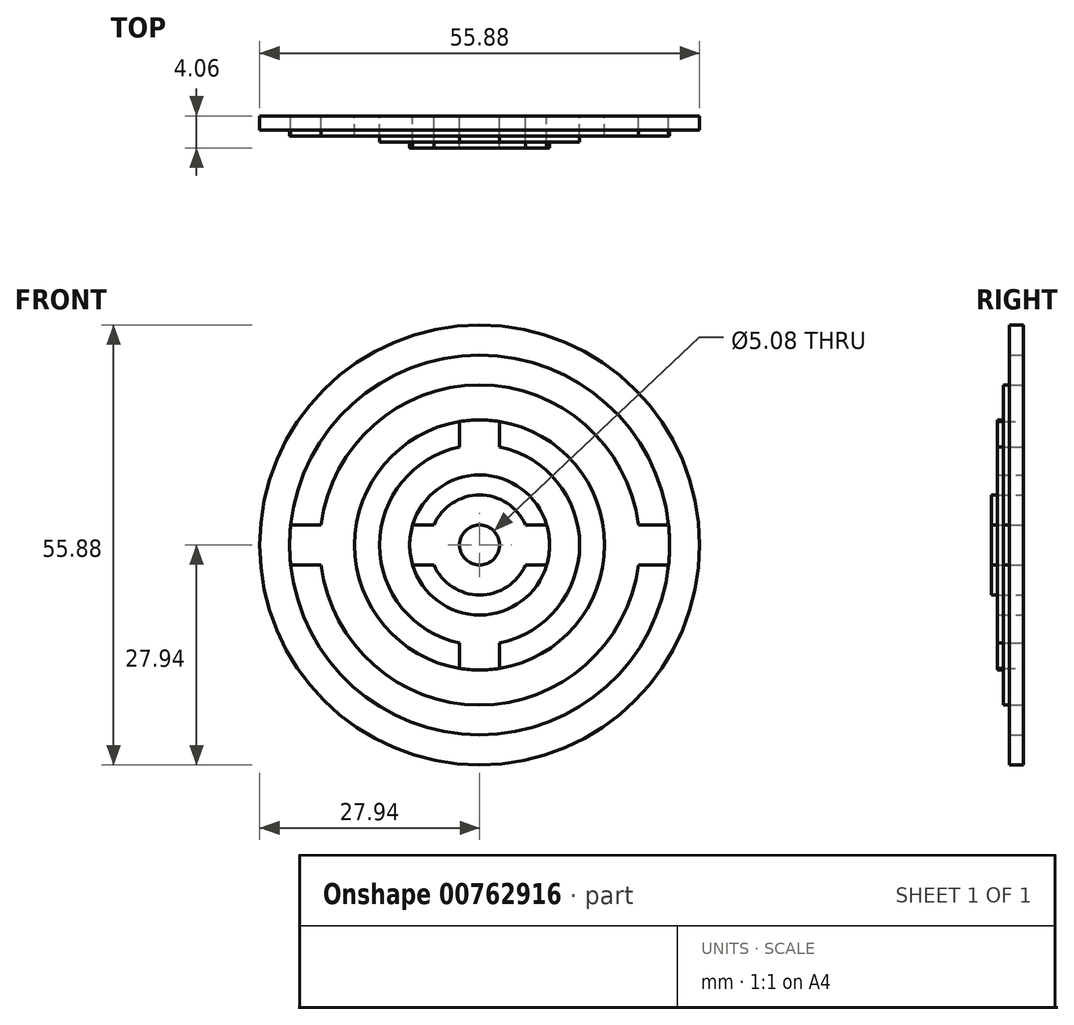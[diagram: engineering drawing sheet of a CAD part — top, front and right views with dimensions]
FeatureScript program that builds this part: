
annotation { "Feature Type Name" : "Feature", "Feature Type Description" : "" }
export const myFeature = defineFeature(function(context is Context, id is Id, definition is map)
    precondition{}
    {
        {
            var Q0;
            Q0=qCreatedBy(makeId("Front.planeOp"),FACE);
            var sketch = newSketch(context, id + "F0", { "sketchPlane" : qUnion([Q0])});
            skCircle(sketch, "E0", {"center": v(0, 0) * mm, "radius": 12.7 * mm});
            skCircle(sketch, "E1", {"center": v(0, 0) * mm, "radius": 20.32 * mm});
            skCircle(sketch, "E2", {"center": v(0, 0) * mm, "radius": 2.54 * mm});
            skCircle(sketch, "E3", {"center": v(0, 0) * mm, "radius": 6.35 * mm});
            skCircle(sketch, "E4", {"center": v(0, 0) * mm, "radius": 27.94 * mm});
            skCircle(sketch, "E5", {"center": v(0, 0) * mm, "radius": 8.9 * mm});
            skCircle(sketch, "E6", {"center": v(0, 0) * mm, "radius": 15.88 * mm});
            skCircle(sketch, "E7", {"center": v(0, 0) * mm, "radius": 24.13 * mm});
            skLineSegment(sketch, "E8", {"start": v(-2.54, -5.82) * mm, "end": v(-2.54, -8.52) * mm});
            skLineSegment(sketch, "E9", {"start": v(2.54, -5.82) * mm, "end": v(2.54, -8.52) * mm});
            skLineSegment(sketch, "E10", {"start": v(5.82, -2.54) * mm, "end": v(8.52, -2.54) * mm});
            skLineSegment(sketch, "E11", {"start": v(-5.82, 2.54) * mm, "end": v(-8.52, 2.54) * mm});
            skLineSegment(sketch, "E12", {"start": v(-5.82, -2.54) * mm, "end": v(-8.52, -2.54) * mm});
            skLineSegment(sketch, "E13.trimOffspring", {"start": v(5.82, 2.54) * mm, "end": v(8.52, 2.54) * mm});
            skLineSegment(sketch, "E14.trimOffspring", {"start": v(2.54, 5.82) * mm, "end": v(2.54, 8.52) * mm});
            skLineSegment(sketch, "E15.trimOffspring", {"start": v(-2.54, 5.82) * mm, "end": v(-2.54, 8.52) * mm});
            skPoint(sketch, "E16.orphan", {"position": v(0, -2.54) * mm});
            skPoint(sketch, "E17.start.orphan", {"position": v(2.54, 0) * mm});
            skPoint(sketch, "E18.orphan", {"position": v(0, 2.54) * mm});
            skPoint(sketch, "E19.start.orphan", {"position": v(-2.54, 0) * mm});
            skLineSegment(sketch, "E20.trimOffspring", {"start": v(-12.44, -2.54) * mm, "end": v(-15.67, -2.54) * mm});
            skLineSegment(sketch, "E21.trimOffspring", {"start": v(-12.44, 2.54) * mm, "end": v(-15.67, 2.54) * mm});
            skLineSegment(sketch, "E22.trimOffspring", {"start": v(-2.54, 12.44) * mm, "end": v(-2.54, 15.67) * mm});
            skLineSegment(sketch, "E23.trimOffspring", {"start": v(2.54, 12.44) * mm, "end": v(2.54, 15.67) * mm});
            skLineSegment(sketch, "E24.trimOffspring", {"start": v(12.44, 2.54) * mm, "end": v(15.67, 2.54) * mm});
            skLineSegment(sketch, "E25.trimOffspring", {"start": v(12.44, -2.54) * mm, "end": v(15.67, -2.54) * mm});
            skLineSegment(sketch, "E26.trimOffspring", {"start": v(20.16, -2.54) * mm, "end": v(24, -2.54) * mm});
            skLineSegment(sketch, "E27.trimOffspring", {"start": v(2.54, -12.44) * mm, "end": v(2.54, -15.67) * mm});
            skLineSegment(sketch, "E28.trimOffspring", {"start": v(-2.54, -12.44) * mm, "end": v(-2.54, -15.67) * mm});
            skLineSegment(sketch, "E29.trimOffspring", {"start": v(20.16, 2.54) * mm, "end": v(24, 2.54) * mm});
            skLineSegment(sketch, "E30.trimOffspring", {"start": v(2.54, 20.16) * mm, "end": v(2.54, 24) * mm});
            skLineSegment(sketch, "E31.trimOffspring", {"start": v(-2.54, 20.16) * mm, "end": v(-2.54, 24) * mm});
            skLineSegment(sketch, "E32.trimOffspring", {"start": v(-20.16, 2.54) * mm, "end": v(-24, 2.54) * mm});
            skLineSegment(sketch, "E33.trimOffspring", {"start": v(-20.16, -2.54) * mm, "end": v(-24, -2.54) * mm});
            skLineSegment(sketch, "E34.trimOffspring", {"start": v(-2.54, -20.16) * mm, "end": v(-2.54, -24) * mm});
            skLineSegment(sketch, "E35.trimOffspring", {"start": v(2.54, -20.16) * mm, "end": v(2.54, -24) * mm});
            skSolve(sketch);
        }
        {
            var Q0;
            Q0=makeQuery(id+"F0.imprint","IMPRINT",FACE,{"disambiguationData":[TD([[makeQuery(id+"F0.imprint","IMPRINT",EDGE,{"derivedFrom":sQuery(id+"F0.wireOp",EDGE,"E2")}),-1.0]])]});
            var Q1;
            {var subQ0=sQuery(id+"F0.wireOp",EDGE,"E11");Q1=makeQuery(id+"F0.imprint","IMPRINT",FACE,{"disambiguationData":[TD([[makeQuery(id+"F0.imprint","IMPRINT",EDGE,{"derivedFrom":subQ0}),1.0]])]});}
            var Q2;
            {var subQ0=sQuery(id+"F0.wireOp",EDGE,"E10");Q2=makeQuery(id+"F0.imprint","IMPRINT",FACE,{"disambiguationData":[TD([[makeQuery(id+"F0.imprint","IMPRINT",EDGE,{"derivedFrom":subQ0}),1.0]])]});}
            extrude(context, id + "F1", {"entities" : qUnion([Q0, Q1, Q2]), "depth" : 4.06 * mm, "offsetDistance" : 25.4 * mm});
        }
        {
            var Q0;
            {var subQ0=sQuery(id+"F0.wireOp",EDGE,"E0");var subQ14=makeQuery(id+"F0.imprint","INTERSECT",VERTEX,{"derivedFrom":[subQ0,sQuery(id+"F0.wireOp",EDGE,"E23.trimOffspring")]});Q0=makeQuery(id+"F0.imprint","IMPRINT",FACE,{"disambiguationData":[TD([[makeQuery(id+"F0.imprint","IMPRINT",EDGE,{"disambiguationData":[TD([[subQ14,1.0]])],"derivedFrom":subQ0}),1.0]])]});}
            var Q1;
            {var subQ0=sQuery(id+"F0.wireOp",EDGE,"E27.trimOffspring");Q1=makeQuery(id+"F0.imprint","IMPRINT",FACE,{"disambiguationData":[TD([[makeQuery(id+"F0.imprint","IMPRINT",EDGE,{"derivedFrom":subQ0}),-1.0]])]});}
            var Q2;
            {var subQ0=sQuery(id+"F0.wireOp",EDGE,"E22.trimOffspring");Q2=makeQuery(id+"F0.imprint","IMPRINT",FACE,{"disambiguationData":[TD([[makeQuery(id+"F0.imprint","IMPRINT",EDGE,{"derivedFrom":subQ0}),-1.0]])]});}
            extrude(context, id + "F2", {"entities" : qUnion([Q0, Q1, Q2]), "operationType" : NewBodyOperationType.ADD, "depth" : 3.3 * mm, "offsetDistance" : 25.4 * mm});
        }
        {
            var Q0;
            {var subQ0=sQuery(id+"F0.wireOp",EDGE,"E1");var subQ2=makeQuery(id+"F0.imprint","INTERSECT",VERTEX,{"derivedFrom":[subQ0,sQuery(id+"F0.wireOp",EDGE,"E29.trimOffspring")]});Q0=makeQuery(id+"F0.imprint","IMPRINT",FACE,{"disambiguationData":[TD([[makeQuery(id+"F0.imprint","IMPRINT",EDGE,{"disambiguationData":[TD([[subQ2,-1.0]])],"derivedFrom":subQ0}),1.0]])]});}
            var Q1;
            {var subQ0=sQuery(id+"F0.wireOp",EDGE,"E26.trimOffspring");Q1=makeQuery(id+"F0.imprint","IMPRINT",FACE,{"disambiguationData":[TD([[makeQuery(id+"F0.imprint","IMPRINT",EDGE,{"derivedFrom":subQ0}),1.0]])]});}
            var Q2;
            {var subQ0=sQuery(id+"F0.wireOp",EDGE,"E32.trimOffspring");Q2=makeQuery(id+"F0.imprint","IMPRINT",FACE,{"disambiguationData":[TD([[makeQuery(id+"F0.imprint","IMPRINT",EDGE,{"derivedFrom":subQ0}),1.0]])]});}
            extrude(context, id + "F3", {"entities" : qUnion([Q0, Q1, Q2]), "operationType" : NewBodyOperationType.ADD, "depth" : 2.54 * mm, "offsetDistance" : 25.4 * mm});
        }
        {
            var Q0;
            Q0=makeQuery(id+"F0.imprint","IMPRINT",FACE,{"disambiguationData":[TD([[makeQuery(id+"F0.imprint","IMPRINT",EDGE,{"derivedFrom":sQuery(id+"F0.wireOp",EDGE,"E4")}),1.0]])]});
            extrude(context, id + "F4", {"entities" : qUnion([Q0]), "operationType" : NewBodyOperationType.ADD, "depth" : 1.78 * mm, "offsetDistance" : 25.4 * mm});
        }
    });
